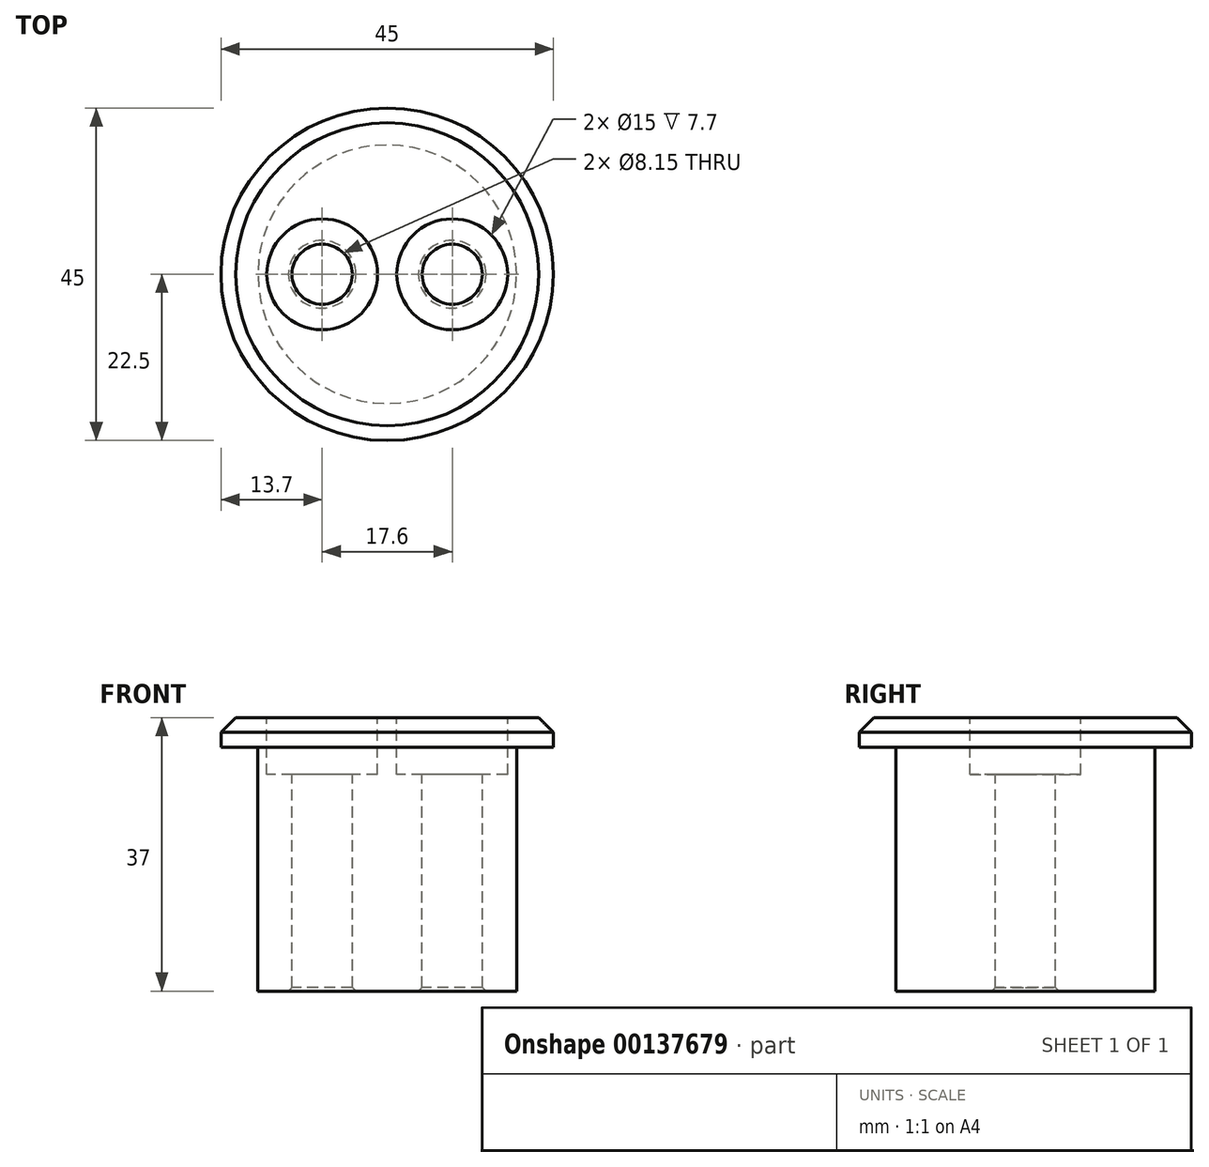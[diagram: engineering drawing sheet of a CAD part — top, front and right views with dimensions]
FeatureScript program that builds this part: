
annotation { "Feature Type Name" : "Feature", "Feature Type Description" : "" }
export const myFeature = defineFeature(function(context is Context, id is Id, definition is map)
    precondition{}
    {
        {
            var Q0;
            Q0=qCreatedBy(makeId("Top.planeOp"),FACE);
            var sketch = newSketch(context, id + "F0", { "sketchPlane" : qUnion([Q0])});
            skCircle(sketch, "E0", {"center": v(0, 0) * mm, "radius": 17.5 * mm});
            skPoint(sketch, "E1.orphan", {"position": v(17.5, 0) * mm});
            skSolve(sketch);
        }
        {
            var Q0;
            Q0 = qSketchRegion(id + "F0", true);
            extrude(context, id + "F1", {"entities" : qUnion([Q0]), "depth" : 33 * mm});
        }
        {
            var Q0;
            Q0=makeQuery(id+"F1.opExtrude","CAP_FACE",FACE,{"disambiguationData":[OSD([sQuery(id+"F0.wireOp",EDGE,"E0")])],"isStart":false});
            var sketch = newSketch(context, id + "F2", { "sketchPlane" : qUnion([Q0])});
            skCircle(sketch, "E2", {"center": v(0, 0) * mm, "radius": 22.5 * mm});
            skSolve(sketch);
        }
        {
            var Q0;
            Q0 = qSketchRegion(id + "F2", true);
            extrude(context, id + "F3", {"entities" : qUnion([Q0]), "operationType" : NewBodyOperationType.ADD, "depth" : 4 * mm});
        }
        {
            var Q0;
            Q0=makeQuery(id+"F3.opExtrude","CAP_FACE",FACE,{"disambiguationData":[OSD([sQuery(id+"F2.wireOp",EDGE,"E2")])],"isStart":false});
            var sketch = newSketch(context, id + "F4", { "sketchPlane" : qUnion([Q0])});
            skCircle(sketch, "E3", {"center": v(-8.8, 0) * mm, "radius": 7.5 * mm});
            skCircle(sketch, "E4", {"center": v(8.8, 0) * mm, "radius": 7.5 * mm});
            skCircle(sketch, "E5", {"center": v(8.8, 0) * mm, "radius": 4.08 * mm});
            skCircle(sketch, "E6.MirrorC", {"center": v(-8.8, 0) * mm, "radius": 4.08 * mm});
            skSolve(sketch);
        }
        {
            var Q0;
            Q0=makeQuery(id+"F4.imprint","IMPRINT",FACE,{"disambiguationData":[TD([[makeQuery(id+"F4.imprint","IMPRINT",EDGE,{"derivedFrom":sQuery(id+"F4.wireOp",EDGE,"E3")}),1.0]])]});
            var Q1;
            Q1=makeQuery(id+"F4.imprint","IMPRINT",FACE,{"disambiguationData":[TD([[makeQuery(id+"F4.imprint","IMPRINT",EDGE,{"derivedFrom":sQuery(id+"F4.wireOp",EDGE,"E4")}),1.0]])]});
            extrude(context, id + "F5", {"entities" : qUnion([Q0, Q1]), "operationType" : NewBodyOperationType.REMOVE, "oppositeDirection" : true, "depth" : 7.7 * mm});
        }
        {
            var Q0;
            Q0=makeQuery(id+"F5.boolean.opBoolean","SPLIT",FACE,{"disambiguationData":[TD([makeQuery(id+"F5.opExtrude","SWEPT_FACE",FACE,{"disambiguationData":[OSD([sQuery(id+"F4.wireOp",EDGE,"E6.MirrorC")])]})])],"derivedFrom":makeQuery(id+"F3.opExtrude","CAP_FACE",FACE,{"disambiguationData":[OSD([sQuery(id+"F2.wireOp",EDGE,"E2")])],"isStart":false})});
            var Q1;
            Q1=makeQuery(id+"F5.boolean.opBoolean","SPLIT",FACE,{"disambiguationData":[TD([makeQuery(id+"F5.opExtrude","SWEPT_FACE",FACE,{"disambiguationData":[OSD([sQuery(id+"F4.wireOp",EDGE,"E5")])]})])],"derivedFrom":makeQuery(id+"F3.opExtrude","CAP_FACE",FACE,{"disambiguationData":[OSD([sQuery(id+"F2.wireOp",EDGE,"E2")])],"isStart":false})});
            extrude(context, id + "F6", {"entities" : qUnion([Q0, Q1]), "operationType" : NewBodyOperationType.REMOVE, "endBound" : BoundingType.THROUGH_ALL, "oppositeDirection" : true, "depth" : 25 * mm});
        }
        {
            var Q0;
            Q0=makeQuery(id+"F3.opExtrude","CAP_EDGE",EDGE,{"disambiguationData":[OSD([sQuery(id+"F2.wireOp",EDGE,"E2")])],"isStart":false});
            chamfer(context, id + "F7", {"entities" : qUnion([Q0]), "width" : 2 * mm, "tangentPropagation" : true});
        }
        {
            var Q0;
            Q0=makeQuery(id+"F5.boolean.opBoolean","COPY",EDGE,{"derivedFrom":makeQuery(id+"F5.opExtrude","CAP_EDGE",EDGE,{"disambiguationData":[OSD([sQuery(id+"F4.wireOp",EDGE,"E3")])],"isStart":true})});
            var Q1;
            Q1=makeQuery(id+"F5.boolean.opBoolean","COPY",EDGE,{"derivedFrom":makeQuery(id+"F5.opExtrude","CAP_EDGE",EDGE,{"disambiguationData":[OSD([sQuery(id+"F4.wireOp",EDGE,"E4")])],"isStart":true})});
            var Q2;
            Q2=makeQuery(id+"F6.boolean.opBoolean","INTERSECT",EDGE,{"derivedFrom":[makeQuery(id+"F1.opExtrude","CAP_FACE",FACE,{"disambiguationData":[OSD([sQuery(id+"F0.wireOp",EDGE,"E0")])],"isStart":true}),makeQuery(id+"F6.opExtrude","SWEPT_FACE",FACE,{"disambiguationData":[OSD([sQuery(id+"F4.wireOp",EDGE,"E6.MirrorC")])]})]});
            var Q3;
            Q3=makeQuery(id+"F6.boolean.opBoolean","INTERSECT",EDGE,{"derivedFrom":[makeQuery(id+"F1.opExtrude","CAP_FACE",FACE,{"disambiguationData":[OSD([sQuery(id+"F0.wireOp",EDGE,"E0")])],"isStart":true}),makeQuery(id+"F6.opExtrude","SWEPT_FACE",FACE,{"disambiguationData":[OSD([sQuery(id+"F4.wireOp",EDGE,"E5")])]})]});
            chamfer(context, id + "F8", {"entities" : qUnion([Q0, Q1, Q2, Q3]), "width" : 0.5 * mm, "tangentPropagation" : true});
        }
    });
